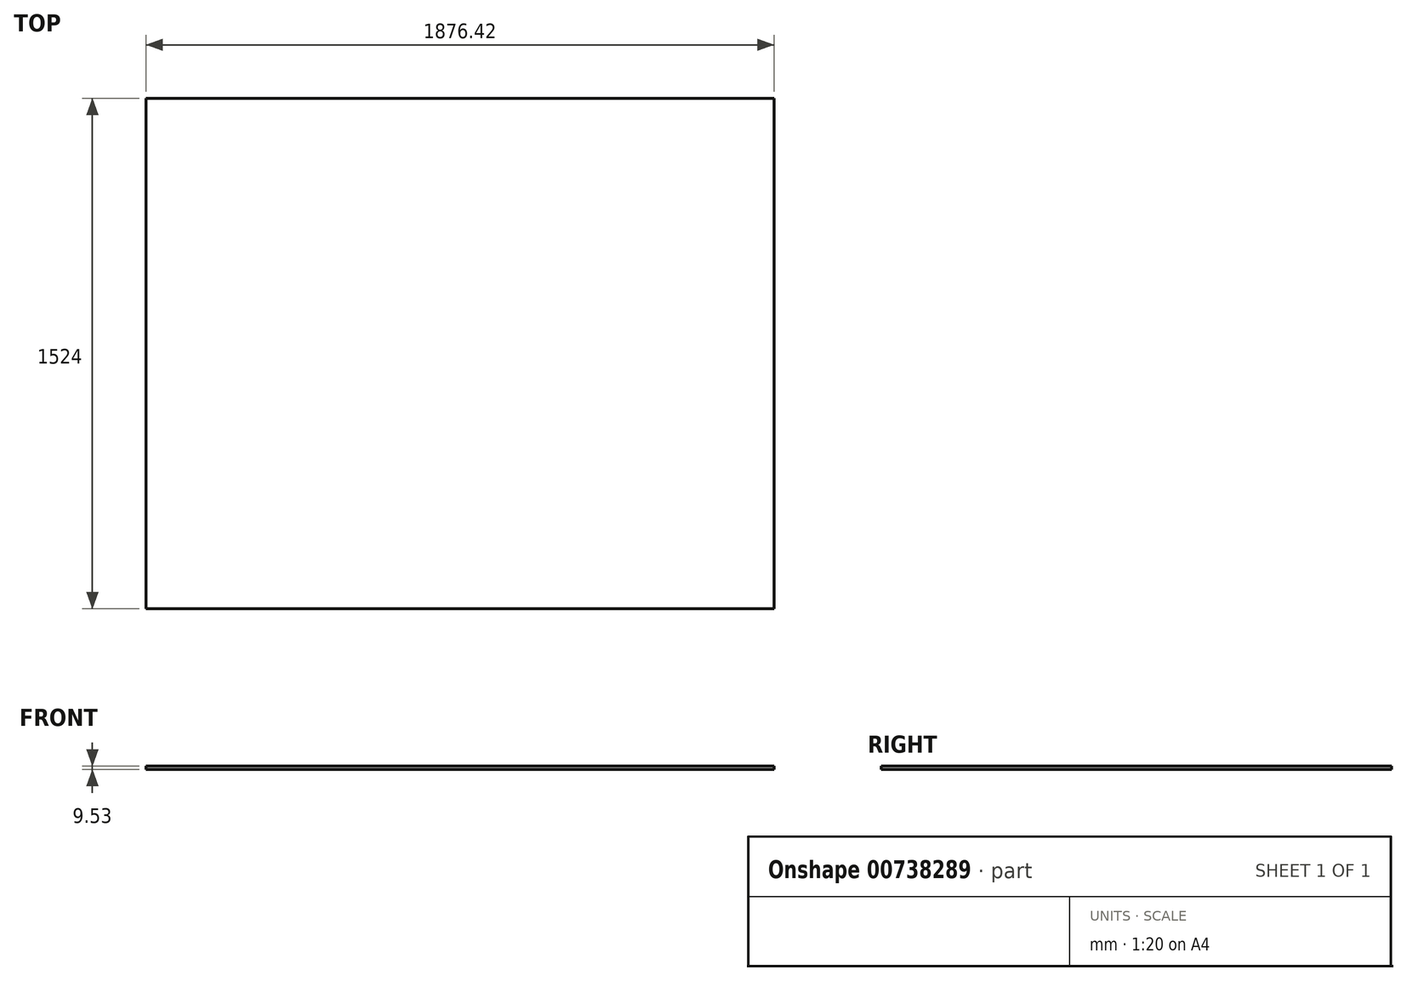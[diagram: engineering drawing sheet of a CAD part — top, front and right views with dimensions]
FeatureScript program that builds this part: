
annotation { "Feature Type Name" : "Feature", "Feature Type Description" : "" }
export const myFeature = defineFeature(function(context is Context, id is Id, definition is map)
    precondition{}
    {
        {
            var Q0;
            Q0=qCreatedBy(makeId("Top.planeOp"),FACE);
            var sketch = newSketch(context, id + "F0", { "sketchPlane" : qUnion([Q0])});
            skLineSegment(sketch, "E0.bottom", {"start": v(-938.21, 762) * mm, "end": v(938.21, 762) * mm});
            skLineSegment(sketch, "E0.top", {"start": v(-938.21, -762) * mm, "end": v(938.21, -762) * mm});
            skLineSegment(sketch, "E0.left", {"start": v(-938.21, 762) * mm, "end": v(-938.21, -762) * mm});
            skLineSegment(sketch, "E0.right", {"start": v(938.21, 762) * mm, "end": v(938.21, -762) * mm});
            skPoint(sketch, "E0.middle", {"position": v(0, 0) * mm});
            skSolve(sketch);
        }
        {
            var Q0;
            Q0=makeQuery(id+"F0.imprint","IMPRINT",FACE,{"disambiguationData":[TD([[makeQuery(id+"F0.imprint","IMPRINT",EDGE,{"derivedFrom":sQuery(id+"F0.wireOp",EDGE,"E0.bottom")}),-1.0]])]});
            extrude(context, id + "F1", {"entities" : qUnion([Q0]), "depth" : 9.52 * mm, "offsetDistance" : 25.4 * mm});
        }
    });
